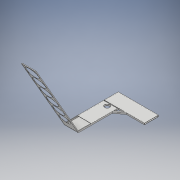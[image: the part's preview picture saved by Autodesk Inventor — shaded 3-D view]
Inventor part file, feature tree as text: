
AUTODESK INVENTOR PART (.ipt)
format: ipt  version: 2018 (Build 220112000, 112)  size: 278,528 bytes
history: native  units: mm
features: extrude x10, sketch x5, plane x2, mirror x2, other x1, projected_geometry x1
ambient origin geometry x8: Origin, YZ Plane, XZ Plane, XY Plane, X Axis, Y Axis, Z Axis, Center Point
bodies: Body1 (feature_tree)
feature tree (21):
  other  "Sólido1"
  sketch  "Boceto1"  dims[d0=51.0mm d1=27.5mm]
  extrude  "Extrusión1"  Depth=27.5mm
  extrude  "Extrusión2"  Depth=1.0mm
  plane  "Plano de trabajo1"
  mirror  "Simetría1"
  sketch  "Boceto2"  dims[d2=1.0mm d3=1.0mm]
  extrude  "Extrusión3"  Depth=0.5mm
  extrude  "Extrusión4"  Depth=1.0mm
  extrude  "Extrusión5"  Depth=0.5mm TaperAngle=0.0deg
  sketch  "Boceto4"  dims[d6=1.0mm d7=1.0mm]
  extrude  "Extrusión6"  Depth=1.21mm TaperAngle=0.0deg
  plane  "Plano de trabajo2"
  extrude  "Extrusión7"  Depth=1.5mm
  mirror  "Simetría2"
  sketch  "Boceto5"  dims[d8=80.0mm d9=0.5mm d10=0.0mm d11=0.96mm d12=0.0mm d13=1.5mm d14=2.42mm d15=0.0mm d16=12.0mm d17=9.0mm d18=4.0mm d19=20.0mm d20=2.92mm d21=0.0mm d22=25.5mm d23=0.0mm d26=30.0deg d29=27.5mm d30=0.0mm d31=1.0mm d32=0.0mm d35=20.5mm d36=2.5mm d37=22.0mm d40=2.5mm d41=22.38mm d44=2.5mm d45=23.0mm d47=2.5mm d48=24.38mm d51=2.5mm d53=25.5mm d54=1.0mm d55=0.0mm d56=1.21mm d57=0.0mm d59=10.0mm d61=6.0mm d62=1.21mm d63=0.0mm]
  extrude  "Extrusión8"  Depth=2.42mm TaperAngle=0.0deg
  extrude  "Extrusión9"  Depth=1.21mm
  extrude  "Extrusión10"  Depth=1.21mm
  sketch  "Boceto3"  dims[d4=27.5mm d5=0.5mm]
  projected_geometry  "Contorno proyectado1"
